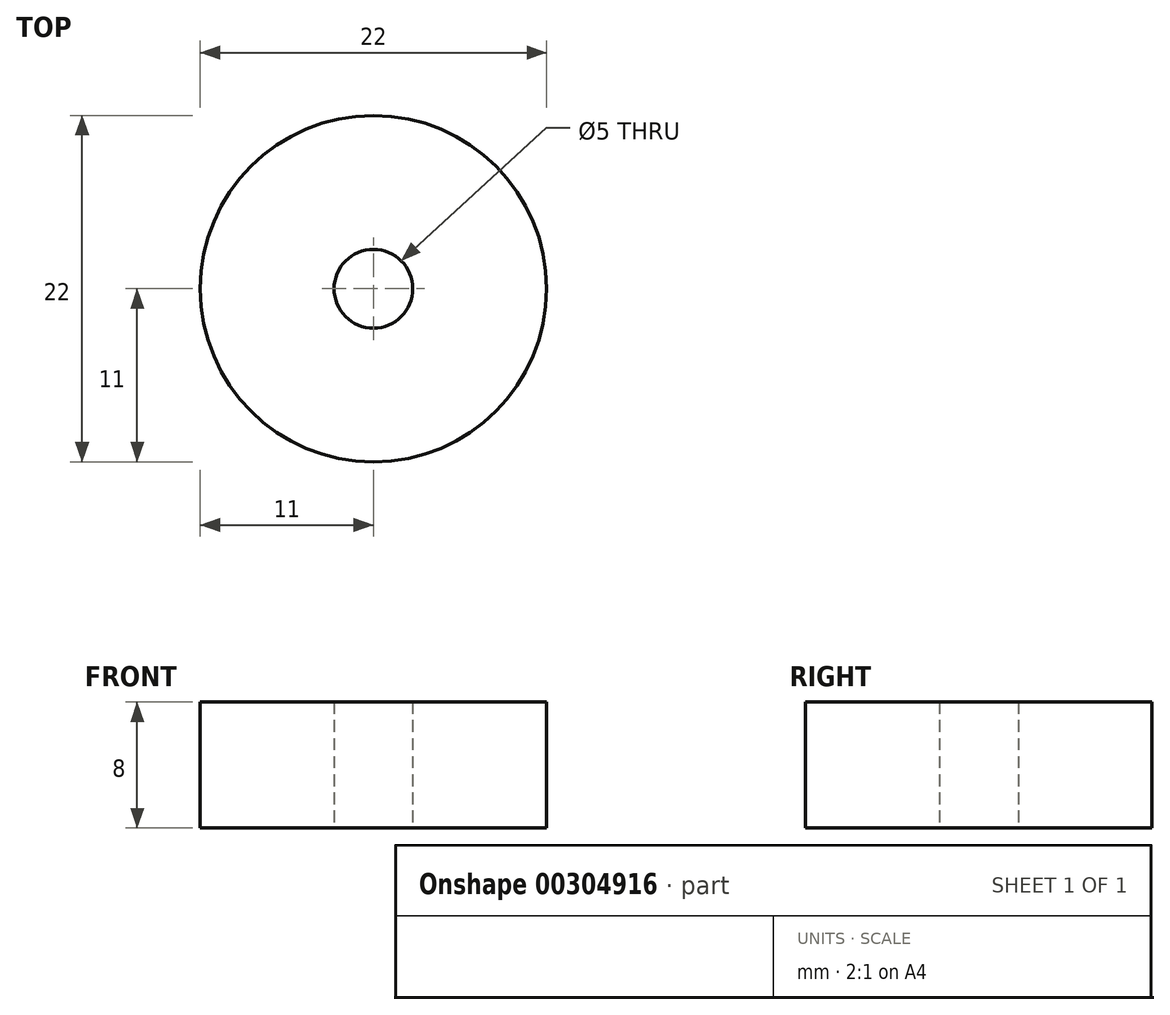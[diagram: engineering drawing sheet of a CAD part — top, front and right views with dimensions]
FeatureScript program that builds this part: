
annotation { "Feature Type Name" : "Feature", "Feature Type Description" : "" }
export const myFeature = defineFeature(function(context is Context, id is Id, definition is map)
    precondition{}
    {
        {
            var Q0;
            Q0=qCreatedBy(makeId("Top.planeOp"),FACE);
            var sketch = newSketch(context, id + "F0", { "sketchPlane" : qUnion([Q0])});
            skCircle(sketch, "E0", {"center": v(0, 0) * mm, "radius": 2.5 * mm});
            skCircle(sketch, "E1", {"center": v(0, 0) * mm, "radius": 11 * mm});
            skSolve(sketch);
        }
        {
            var Q0;
            Q0=makeQuery(id+"F0.imprint","IMPRINT",FACE,{"disambiguationData":[TD([[makeQuery(id+"F0.imprint","IMPRINT",EDGE,{"derivedFrom":sQuery(id+"F0.wireOp",EDGE,"E0")}),-1.0]])]});
            extrude(context, id + "F1", {"entities" : qUnion([Q0]), "depth" : 8 * mm});
        }
    });
